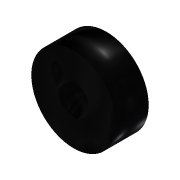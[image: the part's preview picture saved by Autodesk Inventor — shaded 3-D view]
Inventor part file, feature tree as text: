
AUTODESK INVENTOR PART (.ipt)
format: ipt  version: 2019 (Build 230136000, 136)  size: 83,968 bytes
history: native  units: mm
features: extrude x1, sketch x1
ambient origin geometry x8: Origin, YZ Plane, XZ Plane, XY Plane, X Axis, Y Axis, Z Axis, Center Point
bodies: Volumenkörper1 (feature_tree)
feature tree (2):
  extrude  "Extrusion1"  Depth=3.0mm TaperAngle=0.0deg
  sketch  "Skizze1"  dims[d0=7.8mm d1=3.0mm d2=0.0mm]
